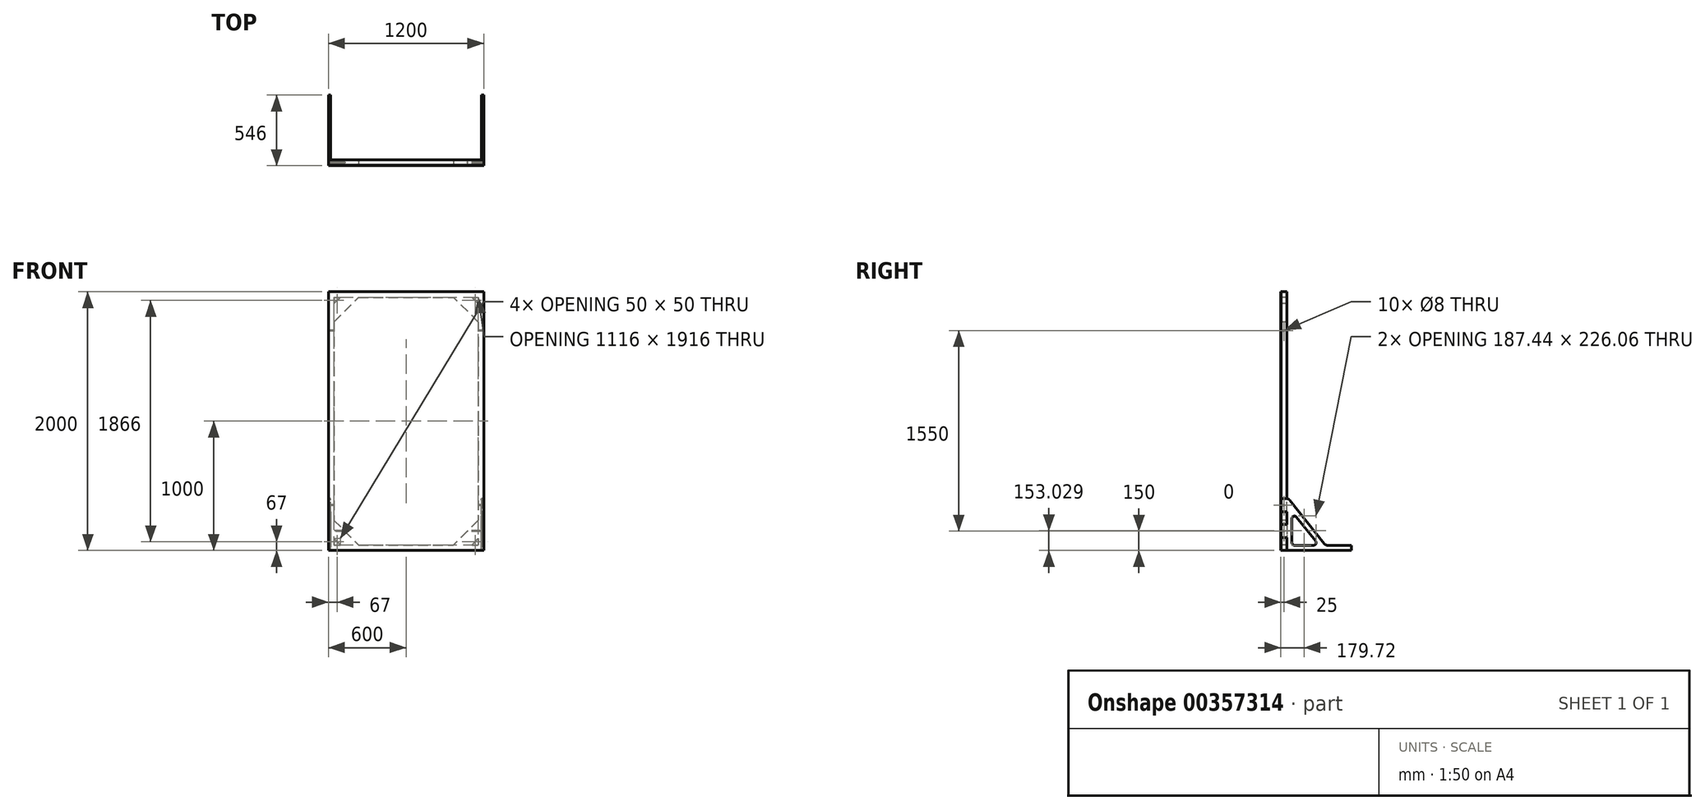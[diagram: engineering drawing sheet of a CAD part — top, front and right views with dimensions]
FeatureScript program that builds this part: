
annotation { "Feature Type Name" : "Feature", "Feature Type Description" : "" }
export const myFeature = defineFeature(function(context is Context, id is Id, definition is map)
    precondition{}
    {
        {
            assignVariable(context, id + "F0", {"name" : "leveys", "anyValue" : 1200});
        }
        {
            assignVariable(context, id + "F1", {"name" : "puu2x2", "anyValue" : 42});
        }
        {
            assignVariable(context, id + "F2", {"name" : "vaneri", "anyValue" : 18});
        }
        {
            var Q0;
            Q0=qCreatedBy(makeId("Front.planeOp"),FACE);
            var sketch = newSketch(context, id + "F3", { "sketchPlane" : qUnion([Q0])});
            skLineSegment(sketch, "E0.bottom", {"start": v(-600, -1000) * mm, "end": v(600, -1000) * mm});
            skLineSegment(sketch, "E0.top", {"start": v(-600, 1000) * mm, "end": v(600, 1000) * mm});
            skLineSegment(sketch, "E0.left", {"start": v(-600, -1000) * mm, "end": v(-600, 1000) * mm});
            skLineSegment(sketch, "E0.right", {"start": v(600, -1000) * mm, "end": v(600, 1000) * mm});
            skPoint(sketch, "E0.middle", {"position": v(0, 0) * mm});
            skLineSegment(sketch, "E1", {"start": v(-558, 1000) * mm, "end": v(-558, -1000) * mm});
            skLineSegment(sketch, "E2", {"start": v(558, 1000) * mm, "end": v(558, -1000) * mm});
            skLineSegment(sketch, "E3", {"start": v(-558, -958) * mm, "end": v(558, -958) * mm});
            skLineSegment(sketch, "E4", {"start": v(-558, 958) * mm, "end": v(558, 958) * mm});
            skLineSegment(sketch, "E5", {"start": v(-558, -908) * mm, "end": v(-508, -958) * mm});
            skLineSegment(sketch, "E6", {"start": v(-558, -766.58) * mm, "end": v(-366.58, -958) * mm});
            skLineSegment(sketch, "E7.MirrorCS", {"start": v(558, -908) * mm, "end": v(508, -958) * mm});
            skLineSegment(sketch, "E8.MirrorCS", {"start": v(558, -766.58) * mm, "end": v(366.58, -958) * mm});
            skLineSegment(sketch, "E9.MirrorCS", {"start": v(-558, 908) * mm, "end": v(-508, 958) * mm});
            skLineSegment(sketch, "E10.MirrorCS", {"start": v(-558, 766.58) * mm, "end": v(-366.58, 958) * mm});
            skLineSegment(sketch, "E11.MirrorCS", {"start": v(558, 766.58) * mm, "end": v(366.58, 958) * mm});
            skLineSegment(sketch, "E12.MirrorCS", {"start": v(558, 908) * mm, "end": v(508, 958) * mm});
            skLineSegment(sketch, "E13", {"start": v(-600, -800) * mm, "end": v(-582, -800) * mm});
            skLineSegment(sketch, "E14", {"start": v(-582, -800) * mm, "end": v(-582, -900) * mm});
            skLineSegment(sketch, "E15", {"start": v(-582, -900) * mm, "end": v(-600, -900) * mm});
            skLineSegment(sketch, "E16", {"start": v(-600, -700) * mm, "end": v(-582, -700) * mm});
            skLineSegment(sketch, "E17", {"start": v(-582, -700) * mm, "end": v(-582, -600) * mm});
            skLineSegment(sketch, "E18", {"start": v(-582, -600) * mm, "end": v(-600, -600) * mm});
            skLineSegment(sketch, "E19.MirrorCS", {"start": v(582, -900) * mm, "end": v(600, -900) * mm});
            skLineSegment(sketch, "E20.MirrorCS", {"start": v(600, -700) * mm, "end": v(582, -700) * mm});
            skLineSegment(sketch, "E21.MirrorCS", {"start": v(600, -800) * mm, "end": v(582, -800) * mm});
            skLineSegment(sketch, "E22.MirrorCS", {"start": v(582, -600) * mm, "end": v(600, -600) * mm});
            skLineSegment(sketch, "E23.MirrorCS", {"start": v(582, -800) * mm, "end": v(582, -900) * mm});
            skLineSegment(sketch, "E24.MirrorCS", {"start": v(582, -700) * mm, "end": v(582, -600) * mm});
            skSolve(sketch);
        }
        {
            var Q0;
            Q0 = qSketchRegion(id + "F3", true);
            var Q1;
            {var subQ3=sQuery(id+"F3.wireOp",EDGE,"E9.MirrorCS");Q1=makeQuery(id+"F3.imprint","IMPRINT",FACE,{"disambiguationData":[TD([[makeQuery(id+"F3.imprint","IMPRINT",EDGE,{"derivedFrom":subQ3}),1.0]])]});}
            var Q2;
            {var subQ0=sQuery(id+"F3.wireOp",EDGE,"E9.MirrorCS");Q2=makeQuery(id+"F3.imprint","IMPRINT",FACE,{"disambiguationData":[TD([[makeQuery(id+"F3.imprint","IMPRINT",EDGE,{"derivedFrom":subQ0}),-1.0]])]});}
            var Q3;
            {var subQ5=sQuery(id+"F3.wireOp",EDGE,"E6");Q3=makeQuery(id+"F3.imprint","IMPRINT",FACE,{"disambiguationData":[TD([[makeQuery(id+"F3.imprint","IMPRINT",EDGE,{"derivedFrom":subQ5}),1.0]])]});}
            var Q4;
            {var subQ0=sQuery(id+"F3.wireOp",EDGE,"E11.MirrorCS");Q4=makeQuery(id+"F3.imprint","IMPRINT",FACE,{"disambiguationData":[TD([[makeQuery(id+"F3.imprint","IMPRINT",EDGE,{"derivedFrom":subQ0}),-1.0]])]});}
            var Q5;
            {var subQ3=sQuery(id+"F3.wireOp",EDGE,"E12.MirrorCS");Q5=makeQuery(id+"F3.imprint","IMPRINT",FACE,{"disambiguationData":[TD([[makeQuery(id+"F3.imprint","IMPRINT",EDGE,{"derivedFrom":subQ3}),-1.0]])]});}
            var Q6;
            {var subQ0=sQuery(id+"F3.wireOp",EDGE,"E7.MirrorCS");Q6=makeQuery(id+"F3.imprint","IMPRINT",FACE,{"disambiguationData":[TD([[makeQuery(id+"F3.imprint","IMPRINT",EDGE,{"derivedFrom":subQ0}),-1.0]])]});}
            var Q7;
            {var subQ3=sQuery(id+"F3.wireOp",EDGE,"E7.MirrorCS");Q7=makeQuery(id+"F3.imprint","IMPRINT",FACE,{"disambiguationData":[TD([[makeQuery(id+"F3.imprint","IMPRINT",EDGE,{"derivedFrom":subQ3}),1.0]])]});}
            var Q8;
            {var subQ0=sQuery(id+"F3.wireOp",EDGE,"E5");Q8=makeQuery(id+"F3.imprint","IMPRINT",FACE,{"disambiguationData":[TD([[makeQuery(id+"F3.imprint","IMPRINT",EDGE,{"derivedFrom":subQ0}),1.0]])]});}
            var Q9;
            {var subQ3=sQuery(id+"F3.wireOp",EDGE,"E5");Q9=makeQuery(id+"F3.imprint","IMPRINT",FACE,{"disambiguationData":[TD([[makeQuery(id+"F3.imprint","IMPRINT",EDGE,{"derivedFrom":subQ3}),-1.0]])]});}
            extrude(context, id + "F4", {"entities" : qUnion([Q0, Q1, Q2, Q3, Q4, Q5, Q6, Q7, Q8, Q9]), "depth" : 4 * mm});
        }
        {
            var Q0;
            {var subQ1=sQuery(id+"F3.wireOp",EDGE,"E1");var subQ5=sQuery(id+"F3.wireOp",EDGE,"E0.bottom");var subQ8=makeQuery(id+"F3.imprint","INTERSECT",VERTEX,{"derivedFrom":[subQ5,subQ1]});Q0=makeQuery(id+"F3.imprint","IMPRINT",FACE,{"disambiguationData":[TD([[makeQuery(id+"F3.imprint","IMPRINT",EDGE,{"disambiguationData":[TD([[subQ8,-1.0]])],"derivedFrom":subQ5}),1.0]])]});}
            var Q1;
            {var subQ1=sQuery(id+"F3.wireOp",EDGE,"E1");var subQ5=sQuery(id+"F3.wireOp",EDGE,"E0.top");var subQ8=makeQuery(id+"F3.imprint","INTERSECT",VERTEX,{"derivedFrom":[subQ5,subQ1]});Q1=makeQuery(id+"F3.imprint","IMPRINT",FACE,{"disambiguationData":[TD([[makeQuery(id+"F3.imprint","IMPRINT",EDGE,{"disambiguationData":[TD([[subQ8,-1.0]])],"derivedFrom":subQ5}),-1.0]])]});}
            var Q2;
            {var subQ14=sQuery(id+"F3.wireOp",EDGE,"E13");Q2=makeQuery(id+"F3.imprint","IMPRINT",FACE,{"disambiguationData":[TD([[makeQuery(id+"F3.imprint","IMPRINT",EDGE,{"derivedFrom":subQ14}),1.0]])]});}
            var Q3;
            {var subQ15=sQuery(id+"F3.wireOp",EDGE,"E19.MirrorCS");Q3=makeQuery(id+"F3.imprint","IMPRINT",FACE,{"disambiguationData":[TD([[makeQuery(id+"F3.imprint","IMPRINT",EDGE,{"derivedFrom":subQ15}),-1.0]])]});}
            var Q4;
            {var subQ0=sQuery(id+"F3.wireOp",EDGE,"E9.MirrorCS");Q4=makeQuery(id+"F3.imprint","IMPRINT",FACE,{"disambiguationData":[TD([[makeQuery(id+"F3.imprint","IMPRINT",EDGE,{"derivedFrom":subQ0}),-1.0]])]});}
            var Q5;
            {var subQ0=sQuery(id+"F3.wireOp",EDGE,"E11.MirrorCS");Q5=makeQuery(id+"F3.imprint","IMPRINT",FACE,{"disambiguationData":[TD([[makeQuery(id+"F3.imprint","IMPRINT",EDGE,{"derivedFrom":subQ0}),-1.0]])]});}
            var Q6;
            {var subQ0=sQuery(id+"F3.wireOp",EDGE,"E7.MirrorCS");Q6=makeQuery(id+"F3.imprint","IMPRINT",FACE,{"disambiguationData":[TD([[makeQuery(id+"F3.imprint","IMPRINT",EDGE,{"derivedFrom":subQ0}),-1.0]])]});}
            var Q7;
            {var subQ0=sQuery(id+"F3.wireOp",EDGE,"E5");Q7=makeQuery(id+"F3.imprint","IMPRINT",FACE,{"disambiguationData":[TD([[makeQuery(id+"F3.imprint","IMPRINT",EDGE,{"derivedFrom":subQ0}),1.0]])]});}
            extrude(context, id + "F5", {"entities" : qUnion([Q0, Q1, Q2, Q3, Q4, Q5, Q6, Q7]), "oppositeDirection" : true, "depth" : (getVariable(context, 'puu2x2')) * mm});
        }
        {
            var Q0;
            {var subQ0=sQuery(id+"F3.wireOp",EDGE,"E0.left");Q0=makeQuery(id+"F5.opExtrude","SWEPT_FACE",FACE,{"disambiguationData":[OSD([subQ0]),TDD([makeQuery(id+"F3.imprint","IMPRINT",EDGE,{"disambiguationData":[TD([[makeQuery(id+"F3.imprint","INTERSECT",VERTEX,{"derivedFrom":[sQuery(id+"F3.wireOp",EDGE,"E0.top"),subQ0]}),1.0]])],"derivedFrom":subQ0})])]});}
            var sketch = newSketch(context, id + "F6", { "sketchPlane" : qUnion([Q0])});
            skCircle(sketch, "E25", {"center": v(-21, 700) * mm, "radius": 4 * mm});
            skCircle(sketch, "E26", {"center": v(-21, -650) * mm, "radius": 4 * mm});
            skCircle(sketch, "E27", {"center": v(-21, -850) * mm, "radius": 4 * mm});
            skSolve(sketch);
        }
        {
            var Q0;
            Q0=makeQuery(id+"F5.opExtrude","SWEPT_FACE",FACE,{"disambiguationData":[OSD([sQuery(id+"F3.wireOp",EDGE,"E23.MirrorCS")])]});
            var sketch = newSketch(context, id + "F7", { "sketchPlane" : qUnion([Q0])});
            skLineSegment(sketch, "E28", {"start": v(42, -800) * mm, "end": v(0, -800) * mm});
            skLineSegment(sketch, "E29", {"start": v(0, -800) * mm, "end": v(0, -900) * mm});
            skLineSegment(sketch, "E30", {"start": v(0, -900) * mm, "end": v(42, -900) * mm});
            skLineSegment(sketch, "E31", {"start": v(42, -900) * mm, "end": v(42, -1000) * mm});
            skLineSegment(sketch, "E32", {"start": v(42, -1000) * mm, "end": v(542, -1000) * mm});
            skLineSegment(sketch, "E33", {"start": v(542, -1000) * mm, "end": v(542, -960) * mm});
            skLineSegment(sketch, "E34", {"start": v(542, -960) * mm, "end": v(356.5, -960) * mm});
            skLineSegment(sketch, "E35", {"start": v(42, -600) * mm, "end": v(0, -600) * mm});
            skLineSegment(sketch, "E36", {"start": v(0, -600) * mm, "end": v(0, -700) * mm});
            skLineSegment(sketch, "E37", {"start": v(0, -700) * mm, "end": v(42, -700) * mm});
            skLineSegment(sketch, "E38", {"start": v(42, -700) * mm, "end": v(42, -800) * mm});
            skArc(sketch, "E39", {"start": v(42, -600) * mm, "mid": v(55.05, -602.99) * mm, "end": v(65.5, -611.36) * mm});
            skLineSegment(sketch, "E40", {"start": v(333, -948.64) * mm, "end": v(65.5, -611.36) * mm});
            skPoint(sketch, "E41.visualSharp", {"position": v(342, -960) * mm});
            skArc(sketch, "E41.filletArc", {"start": v(333, -948.64) * mm, "mid": v(343.44, -957.01) * mm, "end": v(356.5, -960) * mm});
            skLineSegment(sketch, "E42", {"start": v(102, -960) * mm, "end": v(249.56, -960) * mm});
            skLineSegment(sketch, "E43", {"start": v(265.23, -927.57) * mm, "end": v(117.67, -741.5) * mm});
            skLineSegment(sketch, "E44", {"start": v(82, -753.94) * mm, "end": v(82, -940) * mm});
            skPoint(sketch, "E45.visualSharp", {"position": v(82, -696.53) * mm});
            skArc(sketch, "E45.filletArc", {"start": v(117.67, -741.5) * mm, "mid": v(95.42, -735.05) * mm, "end": v(82, -753.94) * mm});
            skPoint(sketch, "E46.visualSharp", {"position": v(82, -960) * mm});
            skArc(sketch, "E46.filletArc", {"start": v(82, -940) * mm, "mid": v(87.86, -954.14) * mm, "end": v(102, -960) * mm});
            skPoint(sketch, "E47.visualSharp", {"position": v(290.95, -960) * mm});
            skArc(sketch, "E47.filletArc", {"start": v(249.56, -960) * mm, "mid": v(267.57, -948.7) * mm, "end": v(265.23, -927.57) * mm});
            skSolve(sketch);
        }
        {
            var Q0;
            Q0 = qSketchRegion(id + "F7", true);
            extrude(context, id + "F8", {"entities" : qUnion([Q0]), "depth" : (getVariable(context, 'vaneri')) * mm});
        }
        {
            var Q0;
            Q0=makeQuery(id+"F8.opExtrude","SWEPT_BODY",BODY,{"disambiguationData":[OSD([sQuery(id+"F7.wireOp",EDGE,"E28"),sQuery(id+"F7.wireOp",EDGE,"E29"),sQuery(id+"F7.wireOp",EDGE,"E30"),sQuery(id+"F7.wireOp",EDGE,"E31"),sQuery(id+"F7.wireOp",EDGE,"E32"),sQuery(id+"F7.wireOp",EDGE,"E33"),sQuery(id+"F7.wireOp",EDGE,"E34"),sQuery(id+"F7.wireOp",EDGE,"E35"),sQuery(id+"F7.wireOp",EDGE,"E36"),sQuery(id+"F7.wireOp",EDGE,"E37"),sQuery(id+"F7.wireOp",EDGE,"E38"),sQuery(id+"F7.wireOp",EDGE,"E39"),sQuery(id+"F7.wireOp",EDGE,"E40"),sQuery(id+"F7.wireOp",EDGE,"E41.filletArc"),sQuery(id+"F7.wireOp",EDGE,"E42"),sQuery(id+"F7.wireOp",EDGE,"E43"),sQuery(id+"F7.wireOp",EDGE,"E44"),sQuery(id+"F7.wireOp",EDGE,"E45.filletArc"),sQuery(id+"F7.wireOp",EDGE,"E46.filletArc"),sQuery(id+"F7.wireOp",EDGE,"E47.filletArc")])]});
            var Q1;
            Q1=qCreatedBy(makeId("Right.planeOp"),FACE);
            mirror(context, id + "F9", {"entities" : qUnion([Q0]), "mirrorPlane" : qUnion([Q1])});
        }
        {
            var Q0;
            Q0 = qSketchRegion(id + "F6", true);
            extrude(context, id + "F10", {"entities" : qUnion([Q0]), "operationType" : NewBodyOperationType.REMOVE, "oppositeDirection" : true, "depth" : (getVariable(context, 'leveys')) * mm});
        }
    });
